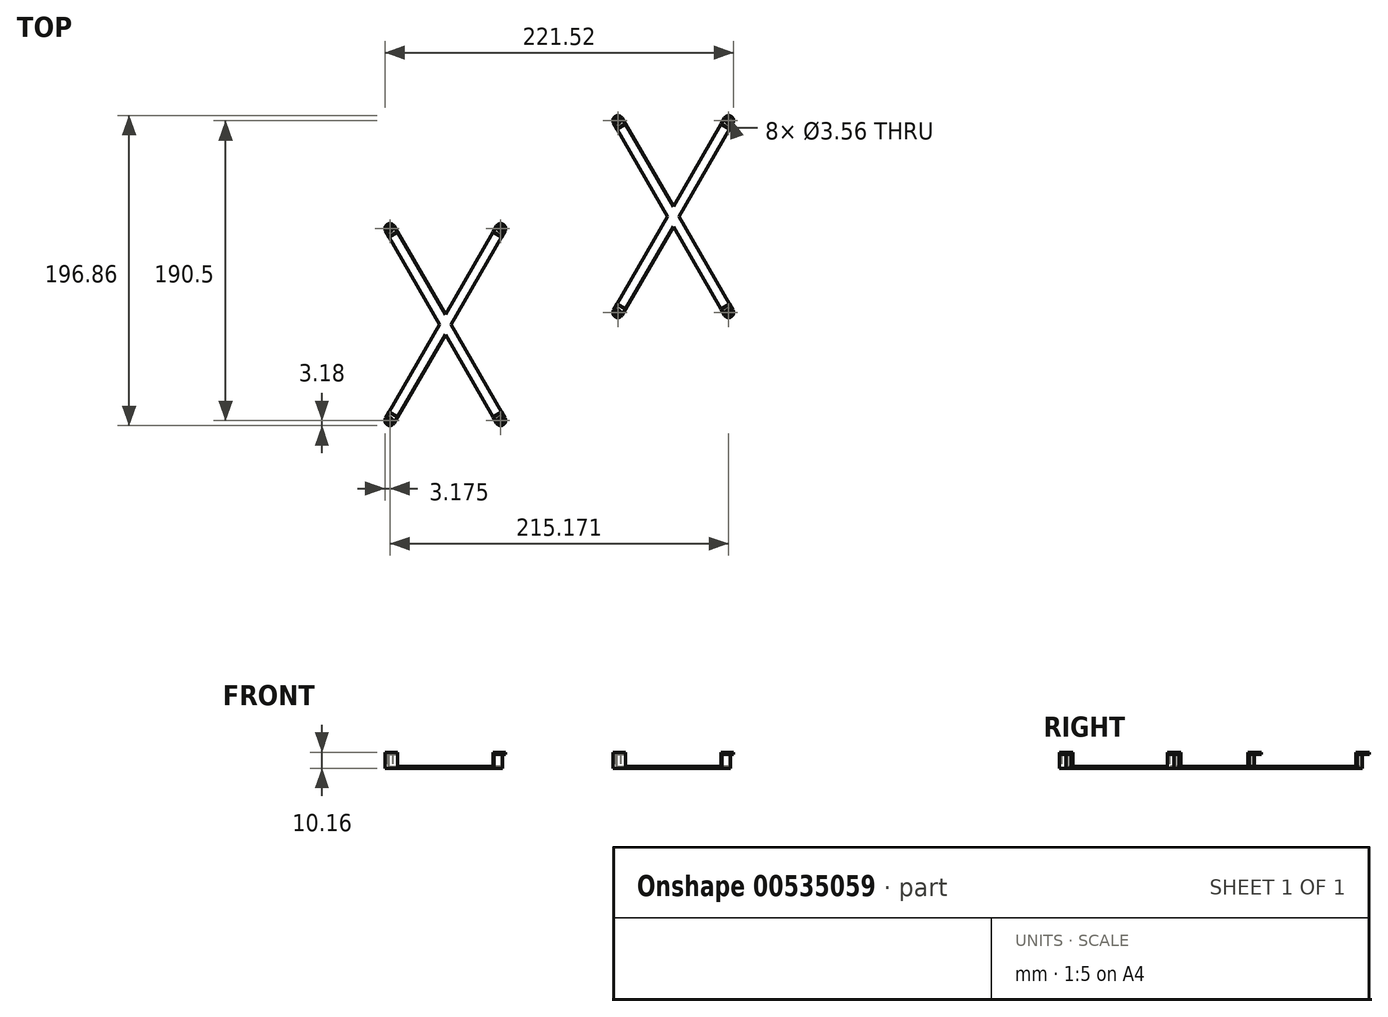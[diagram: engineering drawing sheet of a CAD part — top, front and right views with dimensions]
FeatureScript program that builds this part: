
annotation { "Feature Type Name" : "Feature", "Feature Type Description" : "" }
export const myFeature = defineFeature(function(context is Context, id is Id, definition is map)
    precondition{}
    {
        {
            var Q0;
            Q0=qCreatedBy(makeId("Top.planeOp"),FACE);
            var sketch = newSketch(context, id + "F0", { "sketchPlane" : qUnion([Q0])});
            skCircle(sketch, "E0.0", {"center": v(35.2, -60.96) * mm, "radius": 1.78 * mm});
            skCircle(sketch, "E1.0", {"center": v(-35.2, -60.96) * mm, "radius": 1.78 * mm});
            skCircle(sketch, "E2.0", {"center": v(-35.2, 60.96) * mm, "radius": 1.78 * mm});
            skCircle(sketch, "E3.0", {"center": v(35.2, 60.96) * mm, "radius": 1.78 * mm});
            skLineSegment(sketch, "E4", {"start": v(-35.2, 60.96) * mm, "end": v(35.2, -60.96) * mm});
            skLineSegment(sketch, "E5", {"start": v(35.2, 60.96) * mm, "end": v(-35.2, -60.96) * mm});
            skCircle(sketch, "E6", {"center": v(-35.2, 60.96) * mm, "radius": 3.18 * mm});
            skLineSegment(sketch, "E7", {"start": v(-35.2, 60.96) * mm, "end": v(-64.1, 44.27) * mm});
            skLineSegment(sketch, "E8", {"start": v(-37.94, 59.37) * mm, "end": v(-3.67, 0) * mm});
            skLineSegment(sketch, "E9", {"start": v(-37.94, 59.37) * mm, "end": v(-4.94, 78.43) * mm});
            skLineSegment(sketch, "E10", {"start": v(-32.45, 62.55) * mm, "end": v(0, 6.35) * mm});
            skLineSegment(sketch, "E11", {"start": v(0, 0) * mm, "end": v(0, 28.1) * mm});
            skLineSegment(sketch, "E12", {"start": v(0, 28.1) * mm, "end": v(0, 0) * mm});
            skLineSegment(sketch, "E13", {"start": v(23.57, 0) * mm, "end": v(0, 0) * mm});
            skLineSegment(sketch, "E14.MirrorCS", {"start": v(-32.45, -62.55) * mm, "end": v(0, -6.35) * mm});
            skLineSegment(sketch, "E15.MirrorCS", {"start": v(-37.94, -59.37) * mm, "end": v(-3.67, 0) * mm});
            skCircle(sketch, "E16.MirrorC", {"center": v(-35.2, -60.96) * mm, "radius": 3.18 * mm});
            skLineSegment(sketch, "E17.MirrorCS", {"start": v(32.45, 62.55) * mm, "end": v(0, 6.35) * mm});
            skLineSegment(sketch, "E18.MirrorCS", {"start": v(37.94, 59.37) * mm, "end": v(3.67, 0) * mm});
            skLineSegment(sketch, "E19.MirrorCS", {"start": v(32.45, -62.55) * mm, "end": v(0, -6.35) * mm});
            skLineSegment(sketch, "E20.MirrorCS", {"start": v(37.94, -59.37) * mm, "end": v(3.67, 0) * mm});
            skCircle(sketch, "E21.MirrorC", {"center": v(35.2, 60.96) * mm, "radius": 3.18 * mm});
            skCircle(sketch, "E22.MirrorC", {"center": v(35.2, -60.96) * mm, "radius": 3.18 * mm});
            skSolve(sketch);
        }
        {
            var Q0;
            Q0 = qSketchRegion(id + "F0", true);
            extrude(context, id + "F1", {"entities" : qUnion([Q0]), "depth" : 10.16 * mm, "offsetDistance" : 25.4 * mm});
        }
        {
            var Q0;
            Q0=makeQuery(id+"F1.opExtrude","CAP_FACE",FACE,{"disambiguationData":[OSD([sQuery(id+"F0.wireOp",EDGE,"E0.0"),sQuery(id+"F0.wireOp",EDGE,"E1.0"),sQuery(id+"F0.wireOp",EDGE,"E2.0"),sQuery(id+"F0.wireOp",EDGE,"E3.0"),sQuery(id+"F0.wireOp",EDGE,"E6"),sQuery(id+"F0.wireOp",EDGE,"E8"),sQuery(id+"F0.wireOp",EDGE,"E10"),sQuery(id+"F0.wireOp",EDGE,"E14.MirrorCS"),sQuery(id+"F0.wireOp",EDGE,"E15.MirrorCS"),sQuery(id+"F0.wireOp",EDGE,"E16.MirrorC"),sQuery(id+"F0.wireOp",EDGE,"E17.MirrorCS"),sQuery(id+"F0.wireOp",EDGE,"E18.MirrorCS"),sQuery(id+"F0.wireOp",EDGE,"E19.MirrorCS"),sQuery(id+"F0.wireOp",EDGE,"E20.MirrorCS"),sQuery(id+"F0.wireOp",EDGE,"E21.MirrorC"),sQuery(id+"F0.wireOp",EDGE,"E22.MirrorC")])],"isStart":false});
            var sketch = newSketch(context, id + "F2", { "sketchPlane" : qUnion([Q0])});
            skLineSegment(sketch, "E23", {"start": v(-35.77, 55.6) * mm, "end": v(-30.27, 58.78) * mm});
            skLineSegment(sketch, "E24", {"start": v(-33.02, 57.2) * mm, "end": v(0, 0) * mm});
            skLineSegment(sketch, "E25", {"start": v(-30.27, 58.78) * mm, "end": v(0, 6.35) * mm});
            skLineSegment(sketch, "E26", {"start": v(0, 6.35) * mm, "end": v(30.27, 58.78) * mm});
            skLineSegment(sketch, "E27", {"start": v(30.27, 58.78) * mm, "end": v(35.77, 55.6) * mm});
            skLineSegment(sketch, "E28", {"start": v(35.77, 55.6) * mm, "end": v(3.67, 0) * mm});
            skLineSegment(sketch, "E29", {"start": v(-35.77, 55.6) * mm, "end": v(-3.67, 0) * mm});
            skLineSegment(sketch, "E30", {"start": v(3.67, 0) * mm, "end": v(14.6, 0) * mm});
            skLineSegment(sketch, "E31.MirrorCS", {"start": v(35.77, -55.6) * mm, "end": v(3.67, 0) * mm});
            skLineSegment(sketch, "E32.MirrorCS", {"start": v(0, -6.35) * mm, "end": v(30.27, -58.78) * mm});
            skLineSegment(sketch, "E33.MirrorCS", {"start": v(-30.27, -58.78) * mm, "end": v(0, -6.35) * mm});
            skLineSegment(sketch, "E34.MirrorCS", {"start": v(-35.77, -55.6) * mm, "end": v(-3.67, 0) * mm});
            skLineSegment(sketch, "E35.MirrorCS", {"start": v(30.27, -58.78) * mm, "end": v(35.77, -55.6) * mm});
            skLineSegment(sketch, "E36.MirrorCS", {"start": v(-35.77, -55.6) * mm, "end": v(-30.27, -58.78) * mm});
            skSolve(sketch);
        }
        {
            var Q0;
            Q0 = qSketchRegion(id + "F2", true);
            extrude(context, id + "F3", {"entities" : qUnion([Q0]), "operationType" : NewBodyOperationType.REMOVE, "oppositeDirection" : true, "depth" : 8.9 * mm, "offsetDistance" : 25.4 * mm});
        }
        {
            var Q0;
            Q0=makeQuery(id+"F1.opExtrude","CAP_FACE",FACE,{"disambiguationData":[OSD([sQuery(id+"F0.wireOp",EDGE,"E0.0"),sQuery(id+"F0.wireOp",EDGE,"E1.0"),sQuery(id+"F0.wireOp",EDGE,"E2.0"),sQuery(id+"F0.wireOp",EDGE,"E3.0"),sQuery(id+"F0.wireOp",EDGE,"E6"),sQuery(id+"F0.wireOp",EDGE,"E8"),sQuery(id+"F0.wireOp",EDGE,"E10"),sQuery(id+"F0.wireOp",EDGE,"E14.MirrorCS"),sQuery(id+"F0.wireOp",EDGE,"E15.MirrorCS"),sQuery(id+"F0.wireOp",EDGE,"E16.MirrorC"),sQuery(id+"F0.wireOp",EDGE,"E17.MirrorCS"),sQuery(id+"F0.wireOp",EDGE,"E18.MirrorCS"),sQuery(id+"F0.wireOp",EDGE,"E19.MirrorCS"),sQuery(id+"F0.wireOp",EDGE,"E20.MirrorCS"),sQuery(id+"F0.wireOp",EDGE,"E21.MirrorC"),sQuery(id+"F0.wireOp",EDGE,"E22.MirrorC")])],"isStart":true});
            var sketch = newSketch(context, id + "F4", { "sketchPlane" : qUnion([Q0])});
            skLineSegment(sketch, "E37", {"start": v(-36.4, 56.7) * mm, "end": v(-30.9, 59.88) * mm});
            skLineSegment(sketch, "E38", {"start": v(-33.66, 58.3) * mm, "end": v(0, 0) * mm});
            skLineSegment(sketch, "E39", {"start": v(30.9, 59.88) * mm, "end": v(36.4, 56.7) * mm});
            skLineSegment(sketch, "E40", {"start": v(3.67, 0) * mm, "end": v(8.65, 0) * mm});
            skLineSegment(sketch, "E41.MirrorCS", {"start": v(30.9, -59.88) * mm, "end": v(36.4, -56.7) * mm});
            skLineSegment(sketch, "E42.MirrorCS", {"start": v(-36.4, -56.7) * mm, "end": v(-30.9, -59.88) * mm});
            skLineSegment(sketch, "E43.0", {"start": v(-32.45, 62.55) * mm, "end": v(0, 6.35) * mm});
            skArc(sketch, "E44.0", {"start": v(-32.45, 62.55) * mm, "mid": v(-36.78, 63.7) * mm, "end": v(-37.94, 59.37) * mm});
            skLineSegment(sketch, "E45.0", {"start": v(-37.94, 59.37) * mm, "end": v(-3.67, 0) * mm});
            skLineSegment(sketch, "E46.0", {"start": v(32.45, 62.55) * mm, "end": v(0, 6.35) * mm});
            skArc(sketch, "E47.0", {"start": v(32.45, 62.55) * mm, "mid": v(36.78, 63.7) * mm, "end": v(37.94, 59.37) * mm});
            skLineSegment(sketch, "E48.0", {"start": v(37.94, 59.37) * mm, "end": v(3.67, 0) * mm});
            skLineSegment(sketch, "E49.0", {"start": v(-32.45, -62.55) * mm, "end": v(0, -6.35) * mm});
            skLineSegment(sketch, "E50.0", {"start": v(-37.94, -59.37) * mm, "end": v(-3.67, 0) * mm});
            skLineSegment(sketch, "E51.0", {"start": v(32.45, -62.55) * mm, "end": v(0, -6.35) * mm});
            skArc(sketch, "E52.0", {"start": v(32.45, -62.55) * mm, "mid": v(36.78, -63.7) * mm, "end": v(37.94, -59.37) * mm});
            skLineSegment(sketch, "E53.0", {"start": v(37.94, -59.37) * mm, "end": v(3.67, 0) * mm});
            skSolve(sketch);
        }
        {
            var Q0;
            {var subQ0=sQuery(id+"F4.wireOp",EDGE,"E44.0");Q0=makeQuery(id+"F4.imprint","IMPRINT",FACE,{"disambiguationData":[TD([[makeQuery(id+"F4.imprint","IMPRINT",EDGE,{"derivedFrom":subQ0}),1.0]])]});}
            var Q1;
            {var subQ2=sQuery(id+"F4.wireOp",EDGE,"E39");Q1=makeQuery(id+"F4.imprint","IMPRINT",FACE,{"disambiguationData":[TD([[makeQuery(id+"F4.imprint","IMPRINT",EDGE,{"derivedFrom":subQ2}),1.0]])]});}
            var Q2;
            {var subQ2=sQuery(id+"F4.wireOp",EDGE,"E41.MirrorCS");Q2=makeQuery(id+"F4.imprint","IMPRINT",FACE,{"disambiguationData":[TD([[makeQuery(id+"F4.imprint","IMPRINT",EDGE,{"derivedFrom":subQ2}),-1.0]])]});}
            var Q3;
            {var subQ2=sQuery(id+"F4.wireOp",EDGE,"E42.MirrorCS");Q3=makeQuery(id+"F4.imprint","IMPRINT",FACE,{"disambiguationData":[TD([[makeQuery(id+"F4.imprint","IMPRINT",EDGE,{"derivedFrom":subQ2}),-1.0]])]});}
            extrude(context, id + "F5", {"entities" : qUnion([Q0, Q1, Q2, Q3]), "operationType" : NewBodyOperationType.REMOVE, "oppositeDirection" : true, "depth" : 8.9 * mm, "offsetDistance" : 25.4 * mm});
        }
        {
            var Q0;
            Q0=makeQuery(id+"F1.opExtrude","SWEPT_BODY",BODY,{"disambiguationData":[OSD([sQuery(id+"F0.wireOp",EDGE,"E0.0"),sQuery(id+"F0.wireOp",EDGE,"E1.0"),sQuery(id+"F0.wireOp",EDGE,"E2.0"),sQuery(id+"F0.wireOp",EDGE,"E3.0"),sQuery(id+"F0.wireOp",EDGE,"E6"),sQuery(id+"F0.wireOp",EDGE,"E8"),sQuery(id+"F0.wireOp",EDGE,"E10"),sQuery(id+"F0.wireOp",EDGE,"E14.MirrorCS"),sQuery(id+"F0.wireOp",EDGE,"E15.MirrorCS"),sQuery(id+"F0.wireOp",EDGE,"E16.MirrorC"),sQuery(id+"F0.wireOp",EDGE,"E17.MirrorCS"),sQuery(id+"F0.wireOp",EDGE,"E18.MirrorCS"),sQuery(id+"F0.wireOp",EDGE,"E19.MirrorCS"),sQuery(id+"F0.wireOp",EDGE,"E20.MirrorCS"),sQuery(id+"F0.wireOp",EDGE,"E21.MirrorC"),sQuery(id+"F0.wireOp",EDGE,"E22.MirrorC")])]});
            transform(context, id + "F6", {"entities" : qUnion([Q0]), "transformType" : TransformType.TRANSLATION_3D, "dx" : 144.78 * mm, "dy" : 68.58 * mm, "dz" : 0 * mm, "makeCopy" : true});
        }
    });
